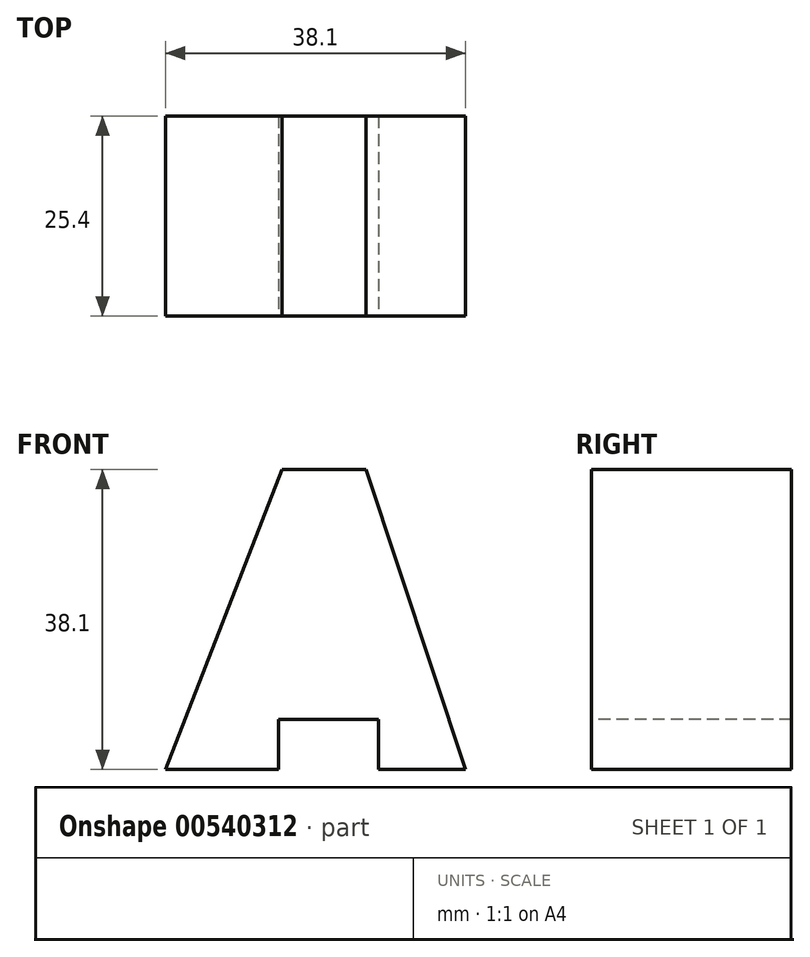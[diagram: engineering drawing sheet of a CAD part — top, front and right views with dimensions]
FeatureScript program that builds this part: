
annotation { "Feature Type Name" : "Feature", "Feature Type Description" : "" }
export const myFeature = defineFeature(function(context is Context, id is Id, definition is map)
    precondition{}
    {
        {
            var Q0;
            Q0=qCreatedBy(makeId("Front.planeOp"),FACE);
            var sketch = newSketch(context, id + "F0", { "sketchPlane" : qUnion([Q0])});
            skLineSegment(sketch, "E0", {"start": v(-38.1, 0) * mm, "end": v(-38.1, 38.1) * mm});
            skLineSegment(sketch, "E1", {"start": v(-38.1, 0) * mm, "end": v(0, 0) * mm});
            skLineSegment(sketch, "E2", {"start": v(0, 0) * mm, "end": v(0, 38.1) * mm});
            skLineSegment(sketch, "E3", {"start": v(-38.1, 38.1) * mm, "end": v(0, 38.1) * mm});
            skSolve(sketch);
        }
        {
            var Q0;
            Q0 = qSketchRegion(id + "F0", true);
            var Q1;
            Q1=makeQuery(id+"F0.imprint","IMPRINT",FACE,{"disambiguationData":[TD([[makeQuery(id+"F0.imprint","IMPRINT",EDGE,{"derivedFrom":sQuery(id+"F0.wireOp",EDGE,"E0")}),-1.0]])]});
            extrude(context, id + "F1", {"entities" : qUnion([Q0, Q1]), "depth" : 25.4 * mm, "offsetDistance" : 25.4 * mm});
        }
        {
            var Q0;
            Q0=makeQuery(id+"F1.opExtrude","CAP_FACE",FACE,{"disambiguationData":[OSD([sQuery(id+"F0.wireOp",EDGE,"E0"),sQuery(id+"F0.wireOp",EDGE,"E1"),sQuery(id+"F0.wireOp",EDGE,"E2"),sQuery(id+"F0.wireOp",EDGE,"E3")])],"isStart":false});
            var sketch = newSketch(context, id + "F2", { "sketchPlane" : qUnion([Q0])});
            skLineSegment(sketch, "E4", {"start": v(-38.1, 0) * mm, "end": v(-23.32, 38.1) * mm});
            skLineSegment(sketch, "E5", {"start": v(0, 0) * mm, "end": v(-12.66, 38.1) * mm});
            skSolve(sketch);
        }
        {
            var Q0;
            Q0 = qSketchRegion(id + "F2", true);
            var Q1;
            {var subQ0=sQuery(id+"F2.wireOp",EDGE,"E4");Q1=makeQuery(id+"F2.imprint","IMPRINT",FACE,{"disambiguationData":[TD([[makeQuery(id+"F2.imprint","IMPRINT",EDGE,{"derivedFrom":subQ0}),1.0]])]});}
            var Q2;
            {var subQ0=sQuery(id+"F2.wireOp",EDGE,"E5");Q2=makeQuery(id+"F2.imprint","IMPRINT",FACE,{"disambiguationData":[TD([[makeQuery(id+"F2.imprint","IMPRINT",EDGE,{"derivedFrom":subQ0}),-1.0]])]});}
            extrude(context, id + "F3", {"entities" : qUnion([Q0, Q1, Q2]), "operationType" : NewBodyOperationType.REMOVE, "oppositeDirection" : true, "depth" : 25.4 * mm, "offsetDistance" : 25.4 * mm});
        }
        {
            var Q0;
            Q0=makeQuery(id+"F1.opExtrude","CAP_FACE",FACE,{"disambiguationData":[OSD([sQuery(id+"F0.wireOp",EDGE,"E0"),sQuery(id+"F0.wireOp",EDGE,"E1"),sQuery(id+"F0.wireOp",EDGE,"E2"),sQuery(id+"F0.wireOp",EDGE,"E3")])],"isStart":false});
            var sketch = newSketch(context, id + "F4", { "sketchPlane" : qUnion([Q0])});
            skLineSegment(sketch, "E6", {"start": v(-23.72, 0) * mm, "end": v(-23.72, 6.35) * mm});
            skLineSegment(sketch, "E7", {"start": v(-23.72, 6.35) * mm, "end": v(-11.02, 6.35) * mm});
            skLineSegment(sketch, "E8", {"start": v(-11.02, 6.35) * mm, "end": v(-11.02, 0) * mm});
            skSolve(sketch);
        }
        {
            var Q0;
            Q0 = qSketchRegion(id + "F4", true);
            var Q1;
            {var subQ0=sQuery(id+"F4.wireOp",EDGE,"E6");Q1=makeQuery(id+"F4.imprint","IMPRINT",FACE,{"disambiguationData":[TD([[makeQuery(id+"F4.imprint","IMPRINT",EDGE,{"derivedFrom":subQ0}),-1.0]])]});}
            extrude(context, id + "F5", {"entities" : qUnion([Q0, Q1]), "operationType" : NewBodyOperationType.REMOVE, "oppositeDirection" : true, "depth" : 25.4 * mm, "offsetDistance" : 25.4 * mm});
        }
    });
